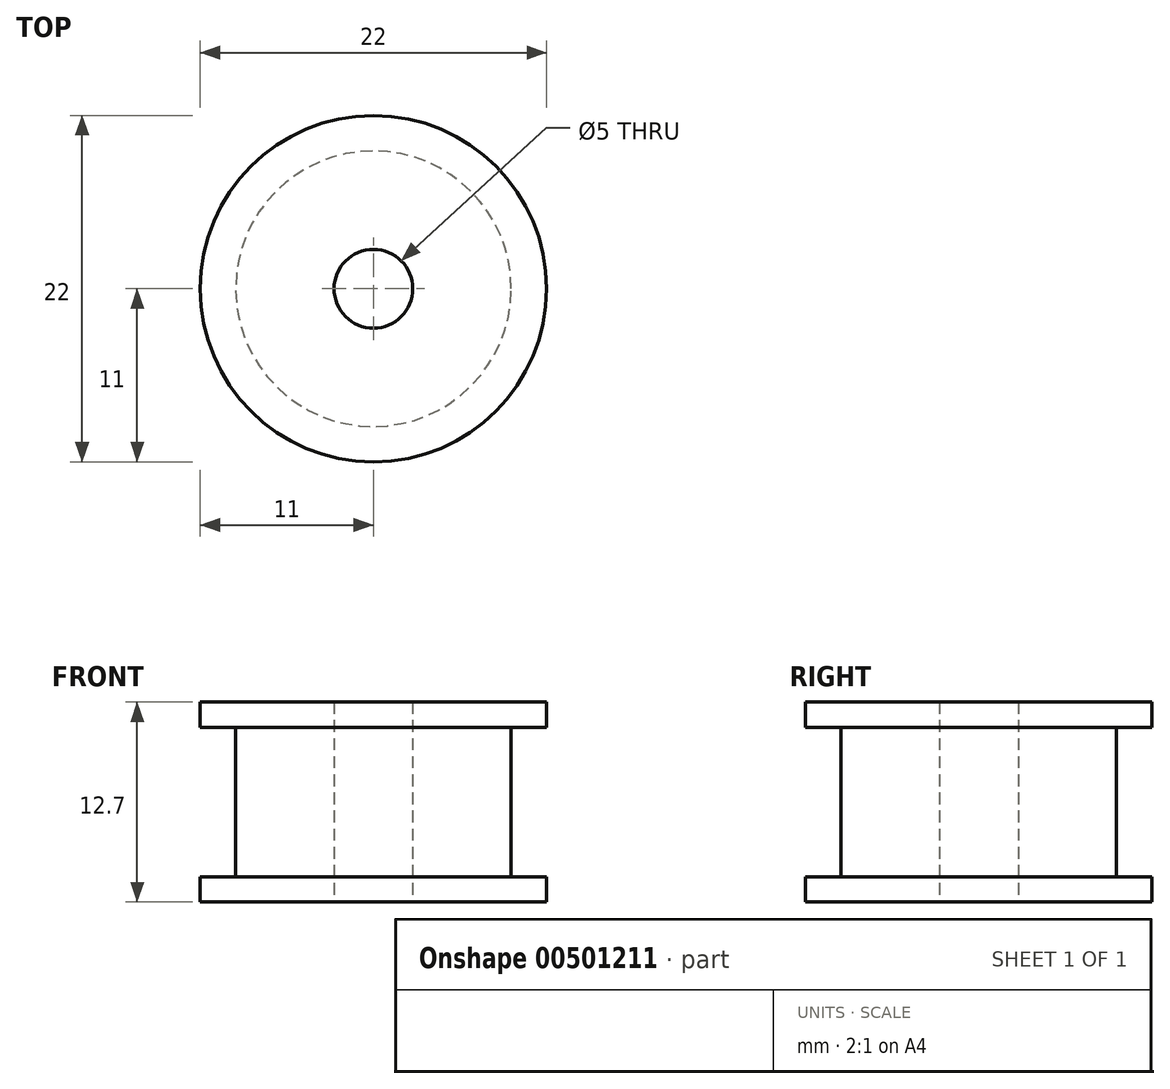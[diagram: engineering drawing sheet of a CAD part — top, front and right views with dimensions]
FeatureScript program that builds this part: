
annotation { "Feature Type Name" : "Feature", "Feature Type Description" : "" }
export const myFeature = defineFeature(function(context is Context, id is Id, definition is map)
    precondition{}
    {
        {
            var Q0;
            Q0=qCreatedBy(makeId("Front.planeOp"),FACE);
            var sketch = newSketch(context, id + "F0", { "sketchPlane" : qUnion([Q0])});
            skLineSegment(sketch, "E0", {"start": v(0, 0) * mm, "end": v(0, 6.4) * mm});
            skLineSegment(sketch, "E1", {"start": v(0, 6.4) * mm, "end": v(-11, 6.4) * mm});
            skLineSegment(sketch, "E2", {"start": v(-11, 6.4) * mm, "end": v(-11, 4.8) * mm});
            skLineSegment(sketch, "E3", {"start": v(-11, 4.8) * mm, "end": v(-8.75, 4.8) * mm});
            skLineSegment(sketch, "E4", {"start": v(-8.75, 4.8) * mm, "end": v(-8.75, -4.7) * mm});
            skLineSegment(sketch, "E5", {"start": v(-8.75, -4.7) * mm, "end": v(-11, -4.7) * mm});
            skLineSegment(sketch, "E6", {"start": v(-11, -4.7) * mm, "end": v(-11, -6.3) * mm});
            skLineSegment(sketch, "E7", {"start": v(-11, -6.3) * mm, "end": v(0, -6.3) * mm});
            skLineSegment(sketch, "E8", {"start": v(0, -6.3) * mm, "end": v(0, 0) * mm});
            skLineSegment(sketch, "E9", {"start": v(-2.5, 6.4) * mm, "end": v(-2.5, -6.3) * mm});
            skPoint(sketch, "E9.endSnap0", {"position": v(-5.5, -6.3) * mm});
            skSolve(sketch);
        }
        {
            var Q0;
            {var subQ0=sQuery(id+"F0.wireOp",EDGE,"E2");Q0=makeQuery(id+"F0.imprint","IMPRINT",FACE,{"disambiguationData":[TD([[makeQuery(id+"F0.imprint","IMPRINT",EDGE,{"derivedFrom":subQ0}),1.0]])]});}
            var Q1;
            Q1=sQuery(id+"F0.wireOp",EDGE,"E0");
            revolve(context, id + "F1", {"entities" : qUnion([Q0]), "axis" : qUnion([Q1]), "revolveType" : RevolveType.FULL});
        }
    });
